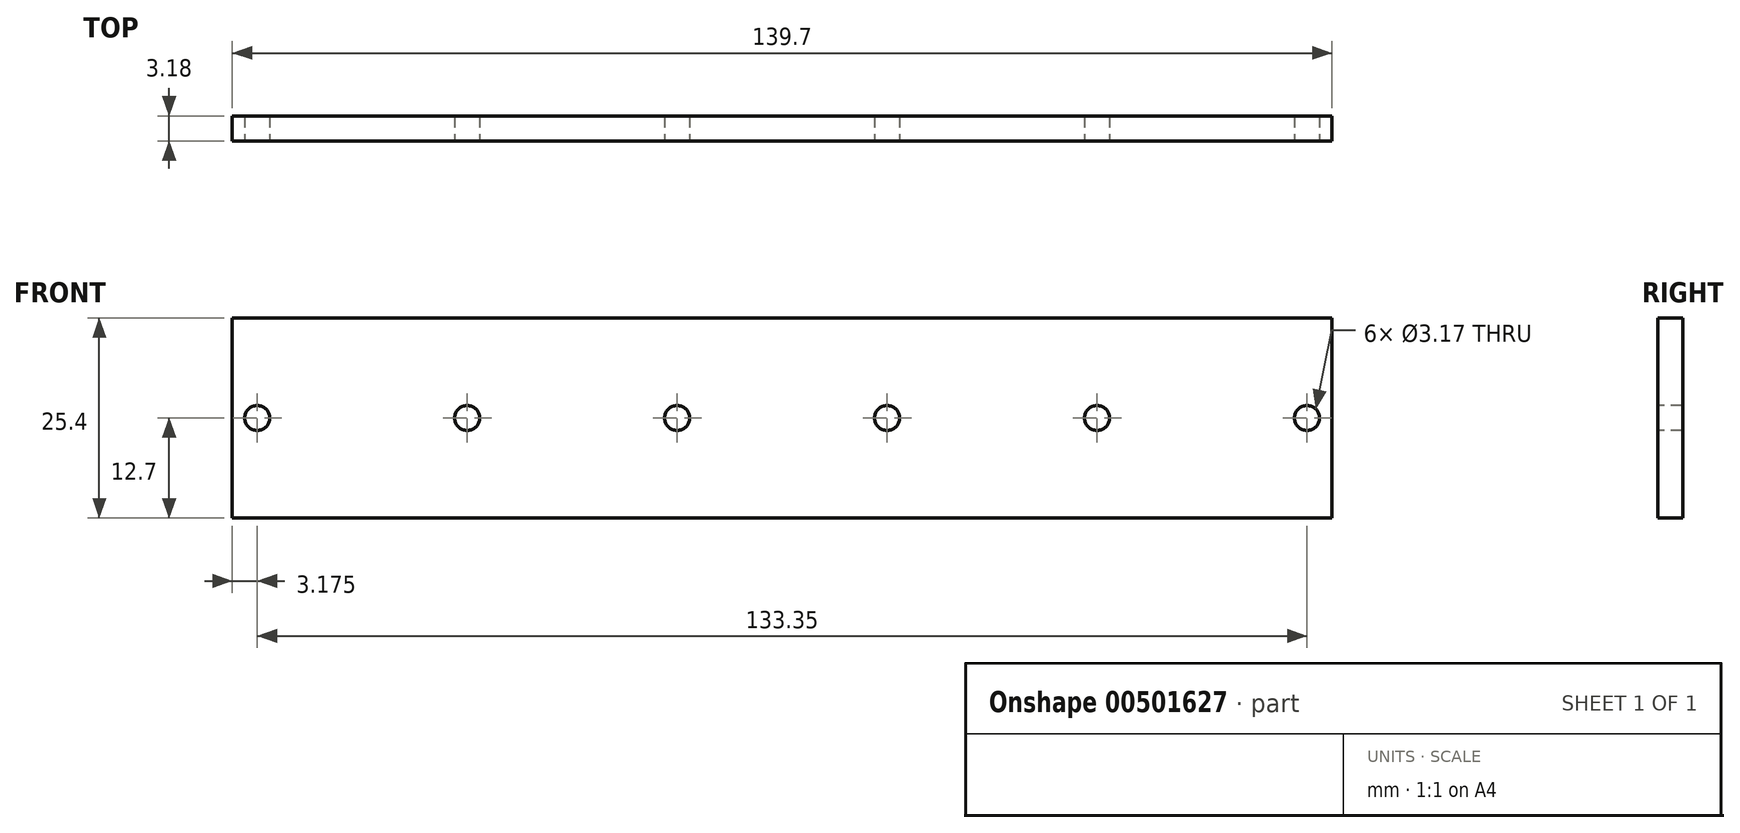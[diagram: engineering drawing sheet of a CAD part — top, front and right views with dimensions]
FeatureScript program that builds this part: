
annotation { "Feature Type Name" : "Feature", "Feature Type Description" : "" }
export const myFeature = defineFeature(function(context is Context, id is Id, definition is map)
    precondition{}
    {
        {
            var Q0;
            Q0=qCreatedBy(makeId("Front.planeOp"),FACE);
            var sketch = newSketch(context, id + "F0", { "sketchPlane" : qUnion([Q0])});
            skLineSegment(sketch, "E0.bottom", {"start": v(69.85, 12.7) * mm, "end": v(-69.85, 12.7) * mm});
            skLineSegment(sketch, "E0.top", {"start": v(69.85, -12.7) * mm, "end": v(-69.85, -12.7) * mm});
            skLineSegment(sketch, "E0.left", {"start": v(69.85, 12.7) * mm, "end": v(69.85, -12.7) * mm});
            skLineSegment(sketch, "E0.right", {"start": v(-69.85, 12.7) * mm, "end": v(-69.85, -12.7) * mm});
            skPoint(sketch, "E0.middle", {"position": v(0, 0) * mm});
            skSolve(sketch);
        }
        {
            var Q0;
            Q0=makeQuery(id+"F0.imprint","IMPRINT",FACE,{"disambiguationData":[TD([[makeQuery(id+"F0.imprint","IMPRINT",EDGE,{"derivedFrom":sQuery(id+"F0.wireOp",EDGE,"E0.bottom")}),1.0]])]});
            extrude(context, id + "F1", {"entities" : qUnion([Q0]), "depth" : 3.17 * mm});
        }
        {
            var Q0;
            Q0=makeQuery(id+"F1.opExtrude","CAP_FACE",FACE,{"disambiguationData":[OSD([sQuery(id+"F0.wireOp",EDGE,"E0.bottom"),sQuery(id+"F0.wireOp",EDGE,"E0.top"),sQuery(id+"F0.wireOp",EDGE,"E0.left"),sQuery(id+"F0.wireOp",EDGE,"E0.right")])],"isStart":false});
            var sketch = newSketch(context, id + "F2", { "sketchPlane" : qUnion([Q0])});
            skCircle(sketch, "E1", {"center": v(-40, 0) * mm, "radius": 1.59 * mm});
            skCircle(sketch, "E2", {"center": v(-13.33, 0) * mm, "radius": 1.59 * mm});
            skCircle(sketch, "E3", {"center": v(13.34, 0) * mm, "radius": 1.59 * mm});
            skCircle(sketch, "E4", {"center": v(40, 0) * mm, "radius": 1.59 * mm});
            skCircle(sketch, "E5", {"center": v(66.68, 0) * mm, "radius": 1.59 * mm});
            skCircle(sketch, "E6", {"center": v(-66.67, 0) * mm, "radius": 1.59 * mm});
            skLineSegment(sketch, "E7", {"start": v(-66.67, 0) * mm, "end": v(-40, 0) * mm});
            skLineSegment(sketch, "E8", {"start": v(-40, 0) * mm, "end": v(-13.33, 0) * mm});
            skLineSegment(sketch, "E9", {"start": v(-13.33, 0) * mm, "end": v(13.34, 0) * mm});
            skLineSegment(sketch, "E10", {"start": v(13.34, 0) * mm, "end": v(40, 0) * mm});
            skLineSegment(sketch, "E11", {"start": v(40, 0) * mm, "end": v(66.68, 0) * mm});
            skLineSegment(sketch, "E12", {"start": v(66.68, 0) * mm, "end": v(69.85, 0) * mm});
            skLineSegment(sketch, "E13", {"start": v(-69.85, 0) * mm, "end": v(-66.67, 0) * mm});
            skSolve(sketch);
        }
        {
            var Q0;
            Q0=qSketchRegion(id+"F2",true);
            extrude(context, id + "F3", {"entities" : qUnion([Q0]), "operationType" : NewBodyOperationType.REMOVE, "oppositeDirection" : true, "depth" : 25.4 * mm});
        }
    });
